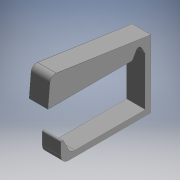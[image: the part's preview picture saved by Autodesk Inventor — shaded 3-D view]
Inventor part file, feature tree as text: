
AUTODESK INVENTOR PART (.ipt)
format: ipt  version: 2018 (Build 220112000, 112)  size: 162,304 bytes
history: native  units: mm
features: extrude x5, other x5, fillet x3
ambient origin geometry x8: Origin, YZ Plane, XZ Plane, XY Plane, X Axis, Y Axis, Z Axis, Center Point
bodies: Solid1 (feature_tree)
feature tree (13):
  extrude  "Key"  Depth=55.0mm
  fillet  "Key Front Rounding"  Radius=15.0mm
  extrude  "Downward Lever Section"  Depth=7.0mm
  extrude  "Horizontal Lever Section"  TaperAngle=0.0deg  [1 undecoded]
  extrude  "Hinge Cut"  Depth=3.0mm
  extrude  "Tube Pincher"  Depth=14.835299mm
  fillet  "Tube Pincher Rounding"  [1 undecoded]
  fillet  "Fillet4"  Radius=1.5mm
  other  "Key Sketch"
  other  "Down Lever Sect Sketch"
  other  "Hinge Cut Sketch"
  other  "Horiz Lever Sect Sketch"
  other  "Tube Pincher Sketch"
note: 2 required parameter values undecoded (feature->parameter linkage not recoverable at this tier; creation-order binding heuristic only, values carry confidence <= 0.55)
